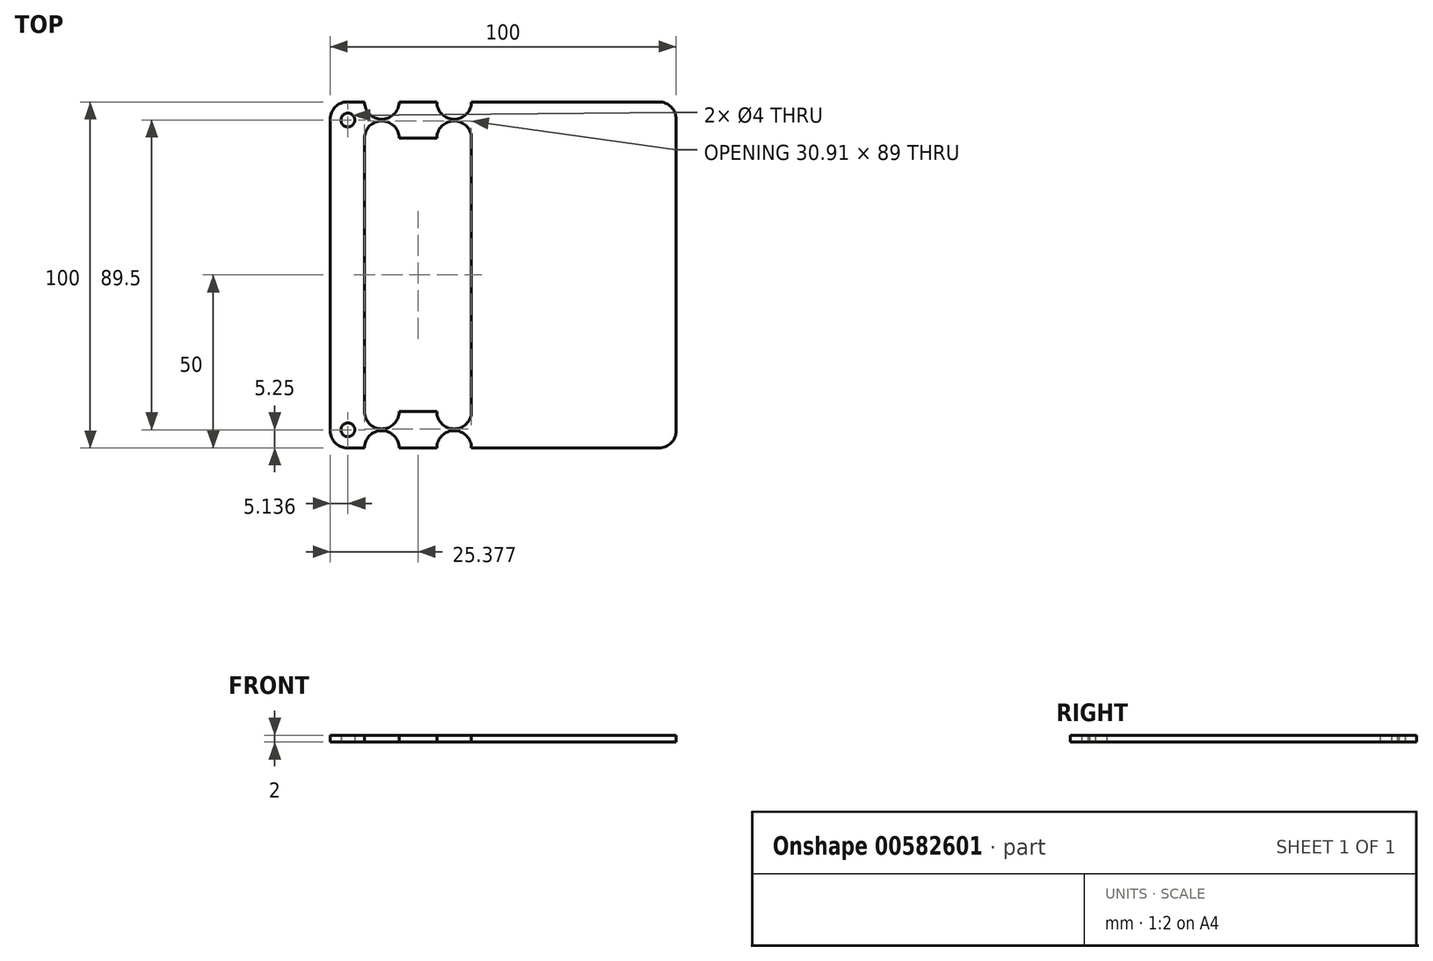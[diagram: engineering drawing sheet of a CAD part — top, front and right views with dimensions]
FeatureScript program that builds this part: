
annotation { "Feature Type Name" : "Feature", "Feature Type Description" : "" }
export const myFeature = defineFeature(function(context is Context, id is Id, definition is map)
    precondition{}
    {
        {
            var Q0;
            Q0=qCreatedBy(makeId("Top.planeOp"),FACE);
            var sketch = newSketch(context, id + "F0", { "sketchPlane" : qUnion([Q0])});
            skLineSegment(sketch, "E0.bottom", {"start": v(50, 50) * mm, "end": v(-50, 50) * mm});
            skLineSegment(sketch, "E0.top", {"start": v(50, -50) * mm, "end": v(-50, -50) * mm});
            skLineSegment(sketch, "E0.left", {"start": v(50, 50) * mm, "end": v(50, -50) * mm});
            skLineSegment(sketch, "E0.right", {"start": v(-50, 50) * mm, "end": v(-50, -50) * mm});
            skPoint(sketch, "E0.middle", {"position": v(0, 0) * mm});
            skLineSegment(sketch, "E1.bottom", {"start": v(-30.08, 39.5) * mm, "end": v(-40.08, 39.5) * mm});
            skLineSegment(sketch, "E1.top", {"start": v(-30.08, -39.5) * mm, "end": v(-40.08, -39.5) * mm});
            skLineSegment(sketch, "E1.left", {"start": v(-30.08, 39.5) * mm, "end": v(-30.08, -39.5) * mm});
            skLineSegment(sketch, "E1.right", {"start": v(-40.08, 39.5) * mm, "end": v(-40.08, -39.5) * mm});
            skPoint(sketch, "E1.middle", {"position": v(-35.08, 0) * mm});
            skCircle(sketch, "E2", {"center": v(-35.08, 39.5) * mm, "radius": 5 * mm});
            skCircle(sketch, "E3", {"center": v(-35.08, -39.5) * mm, "radius": 5 * mm});
            skCircle(sketch, "E4", {"center": v(-35.08, 50) * mm, "radius": 5 * mm});
            skCircle(sketch, "E5", {"center": v(-35.08, -50) * mm, "radius": 5 * mm});
            skLineSegment(sketch, "E6.bottom", {"start": v(-9.17, 39.5) * mm, "end": v(-19.17, 39.5) * mm});
            skLineSegment(sketch, "E6.top", {"start": v(-9.17, -39.5) * mm, "end": v(-19.17, -39.5) * mm});
            skLineSegment(sketch, "E6.left", {"start": v(-9.17, 39.5) * mm, "end": v(-9.17, -39.5) * mm});
            skLineSegment(sketch, "E6.right", {"start": v(-19.17, 39.5) * mm, "end": v(-19.17, -39.5) * mm});
            skPoint(sketch, "E6.middle", {"position": v(-14.17, 0) * mm});
            skCircle(sketch, "E7", {"center": v(-14.17, 39.5) * mm, "radius": 5 * mm});
            skCircle(sketch, "E8", {"center": v(-14.17, -39.5) * mm, "radius": 5 * mm});
            skCircle(sketch, "E9", {"center": v(-14.17, 50) * mm, "radius": 5 * mm});
            skCircle(sketch, "E10", {"center": v(-14.17, -50) * mm, "radius": 5 * mm});
            skLineSegment(sketch, "E11.bottom", {"start": v(-30.08, 39.5) * mm, "end": v(-19.17, 39.5) * mm});
            skLineSegment(sketch, "E11.top", {"start": v(-30.08, -39.5) * mm, "end": v(-19.17, -39.5) * mm});
            skCircle(sketch, "E12", {"center": v(-44.86, -44.75) * mm, "radius": 2 * mm});
            skCircle(sketch, "E13", {"center": v(-44.86, 44.75) * mm, "radius": 2 * mm});
            skPoint(sketch, "E14", {"position": v(-35.08, 44.75) * mm});
            skPoint(sketch, "E15", {"position": v(-35.08, -44.75) * mm});
            skSolve(sketch);
        }
        {
            var Q0;
            {var subQ7=sQuery(id+"F0.wireOp",EDGE,"E0.left");Q0=makeQuery(id+"F0.imprint","IMPRINT",FACE,{"disambiguationData":[TD([[makeQuery(id+"F0.imprint","IMPRINT",EDGE,{"derivedFrom":subQ7}),-1.0]])]});}
            extrude(context, id + "F1", {"entities" : qUnion([Q0]), "depth" : 2 * mm, "offsetDistance" : 25 * mm});
        }
        {
            var Q0;
            Q0=makeQuery(id+"F1.opExtrude","SWEPT_EDGE",EDGE,{"disambiguationData":[OSD([sQuery(id+"F0.wireOp",EDGE,"E0.top"),sQuery(id+"F0.wireOp",EDGE,"E0.left")])]});
            var Q1;
            Q1=makeQuery(id+"F1.opExtrude","SWEPT_EDGE",EDGE,{"disambiguationData":[OSD([sQuery(id+"F0.wireOp",EDGE,"E0.bottom"),sQuery(id+"F0.wireOp",EDGE,"E0.left")])]});
            var Q2;
            Q2=makeQuery(id+"F1.opExtrude","SWEPT_EDGE",EDGE,{"disambiguationData":[OSD([sQuery(id+"F0.wireOp",EDGE,"E0.top"),sQuery(id+"F0.wireOp",EDGE,"E0.right")])]});
            var Q3;
            Q3=makeQuery(id+"F1.opExtrude","SWEPT_EDGE",EDGE,{"disambiguationData":[OSD([sQuery(id+"F0.wireOp",EDGE,"E0.bottom"),sQuery(id+"F0.wireOp",EDGE,"E0.right")])]});
            fillet(context, id + "F2", {"entities" : qUnion([Q0, Q1, Q2, Q3]), "radius" : 5 * mm, "tangentPropagation" : true, "allowEdgeOverflow" : false});
        }
    });
